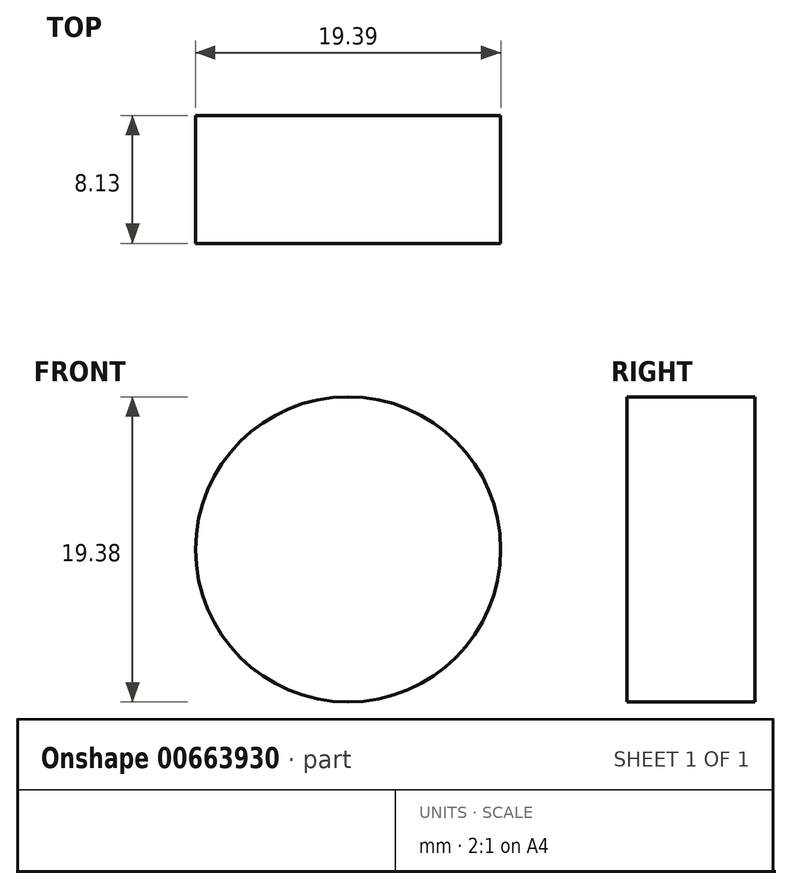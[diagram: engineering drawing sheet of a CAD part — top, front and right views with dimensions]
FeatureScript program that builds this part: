
annotation { "Feature Type Name" : "Feature", "Feature Type Description" : "" }
export const myFeature = defineFeature(function(context is Context, id is Id, definition is map)
    precondition{}
    {
        {
            var Q0;
            Q0=qCreatedBy(makeId("Front.planeOp"),FACE);
            var sketch = newSketch(context, id + "F0", { "sketchPlane" : qUnion([Q0])});
            skCircle(sketch, "E0", {"center": v(-119.83, 6.9) * mm, "radius": 9.7 * mm});
            skSolve(sketch);
        }
        {
            var Q0;
            Q0 = qSketchRegion(id + "F0", true);
            extrude(context, id + "F1", {"entities" : qUnion([Q0]), "depth" : 8.13 * mm, "offsetDistance" : 25.4 * mm});
        }
    });
